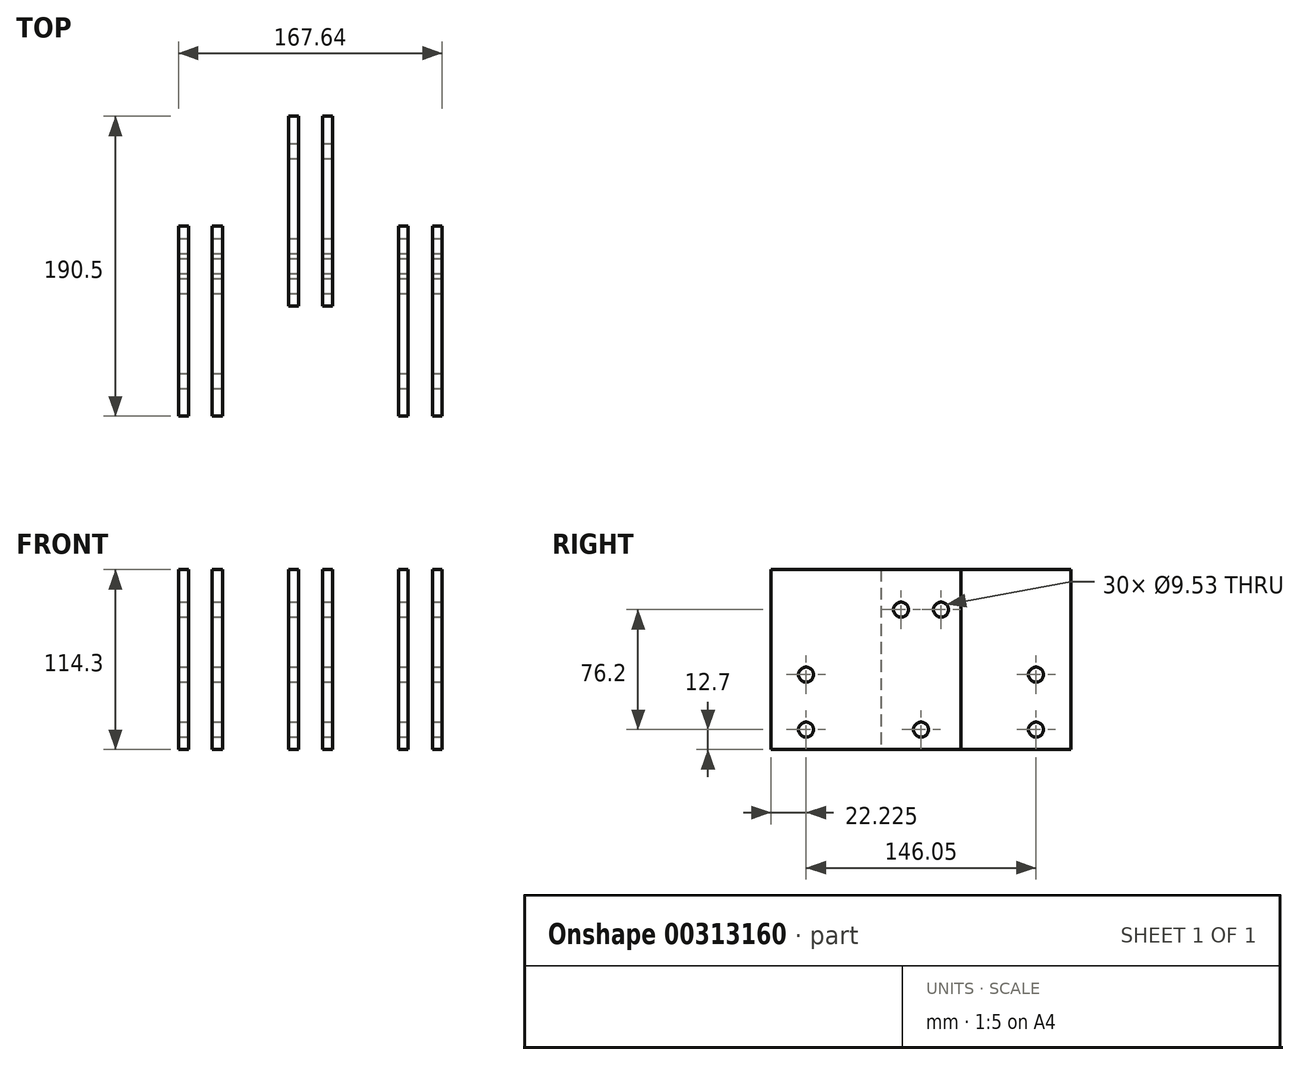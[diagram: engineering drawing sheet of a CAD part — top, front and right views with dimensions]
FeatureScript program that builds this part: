
annotation { "Feature Type Name" : "Feature", "Feature Type Description" : "" }
export const myFeature = defineFeature(function(context is Context, id is Id, definition is map)
    precondition{}
    {
        {
            var Q0;
            Q0=qCreatedBy(makeId("Top.planeOp"),FACE);
            var sketch = newSketch(context, id + "F0", { "sketchPlane" : qUnion([Q0])});
            skLineSegment(sketch, "E0.bottom", {"start": v(0, 120.65) * mm, "end": v(6.35, 120.65) * mm});
            skLineSegment(sketch, "E0.top", {"start": v(0, 0) * mm, "end": v(6.35, 0) * mm});
            skLineSegment(sketch, "E0.left", {"start": v(0, 120.65) * mm, "end": v(0, 0) * mm});
            skLineSegment(sketch, "E0.right", {"start": v(6.35, 120.65) * mm, "end": v(6.35, 0) * mm});
            skLineSegment(sketch, "E1.bottom", {"start": v(21.6, 120.65) * mm, "end": v(27.94, 120.65) * mm});
            skLineSegment(sketch, "E1.top", {"start": v(21.6, 0) * mm, "end": v(27.94, 0) * mm});
            skLineSegment(sketch, "E1.left", {"start": v(21.6, 120.65) * mm, "end": v(21.6, 0) * mm});
            skLineSegment(sketch, "E1.right", {"start": v(27.94, 120.65) * mm, "end": v(27.94, 0) * mm});
            skLineSegment(sketch, "E2.bottom", {"start": v(-69.85, 190.5) * mm, "end": v(-63.5, 190.5) * mm});
            skLineSegment(sketch, "E2.top", {"start": v(-69.85, 69.85) * mm, "end": v(-63.5, 69.85) * mm});
            skLineSegment(sketch, "E2.left", {"start": v(-69.85, 190.5) * mm, "end": v(-69.85, 69.85) * mm});
            skLineSegment(sketch, "E2.right", {"start": v(-63.5, 190.5) * mm, "end": v(-63.5, 69.85) * mm});
            skLineSegment(sketch, "E3.bottom", {"start": v(-48.26, 190.5) * mm, "end": v(-41.9, 190.5) * mm});
            skLineSegment(sketch, "E3.top", {"start": v(-48.26, 69.85) * mm, "end": v(-41.9, 69.85) * mm});
            skLineSegment(sketch, "E3.left", {"start": v(-48.26, 190.5) * mm, "end": v(-48.26, 69.85) * mm});
            skLineSegment(sketch, "E3.right", {"start": v(-41.9, 190.5) * mm, "end": v(-41.9, 69.85) * mm});
            skLineSegment(sketch, "E4.bottom", {"start": v(-139.7, 120.65) * mm, "end": v(-133.35, 120.65) * mm});
            skLineSegment(sketch, "E4.top", {"start": v(-139.7, 0) * mm, "end": v(-133.35, 0) * mm});
            skLineSegment(sketch, "E4.left", {"start": v(-139.7, 120.65) * mm, "end": v(-139.7, 0) * mm});
            skLineSegment(sketch, "E4.right", {"start": v(-133.35, 120.65) * mm, "end": v(-133.35, 0) * mm});
            skLineSegment(sketch, "E5.bottom", {"start": v(-118.1, 120.65) * mm, "end": v(-111.76, 120.65) * mm});
            skLineSegment(sketch, "E5.top", {"start": v(-118.1, 0) * mm, "end": v(-111.76, 0) * mm});
            skLineSegment(sketch, "E5.left", {"start": v(-118.1, 120.65) * mm, "end": v(-118.1, 0) * mm});
            skLineSegment(sketch, "E5.right", {"start": v(-111.76, 120.65) * mm, "end": v(-111.76, 0) * mm});
            skSolve(sketch);
        }
        {
            var Q0;
            Q0=qSketchRegion(id+"F0",true);
            extrude(context, id + "F1", {"entities" : qUnion([Q0]), "endBound" : BoundingType.SYMMETRIC, "depth" : 114.3 * mm});
        }
        {
            var Q0;
            Q0=qCreatedBy(makeId("Right.planeOp"),FACE);
            var sketch = newSketch(context, id + "F2", { "sketchPlane" : qUnion([Q0])});
            skCircle(sketch, "E6", {"center": v(82.55, 31.75) * mm, "radius": 4.76 * mm});
            skCircle(sketch, "E7", {"center": v(82.55, 6.35) * mm, "radius": 4.76 * mm, "construction": true});
            skCircle(sketch, "E8", {"center": v(168.28, -44.45) * mm, "radius": 4.76 * mm});
            skCircle(sketch, "E9", {"center": v(168.28, -9.52) * mm, "radius": 4.76 * mm});
            skLineSegment(sketch, "E10", {"start": v(95.25, 31.75) * mm, "end": v(95.25, 6.35) * mm, "construction": true});
            skCircle(sketch, "E11.MirrorC", {"center": v(22.23, -44.45) * mm, "radius": 4.76 * mm});
            skCircle(sketch, "E12.MirrorC", {"center": v(22.23, -9.53) * mm, "radius": 4.76 * mm});
            skCircle(sketch, "E13", {"center": v(107.95, 31.75) * mm, "radius": 4.76 * mm});
            skLineSegment(sketch, "E14.bottom", {"start": v(82.55, 31.75) * mm, "end": v(107.95, 31.75) * mm, "construction": true});
            skLineSegment(sketch, "E14.top", {"start": v(82.55, 6.35) * mm, "end": v(107.95, 6.35) * mm, "construction": true});
            skLineSegment(sketch, "E14.left", {"start": v(82.55, 31.75) * mm, "end": v(82.55, 6.35) * mm, "construction": true});
            skLineSegment(sketch, "E14.right", {"start": v(107.95, 31.75) * mm, "end": v(107.95, 6.35) * mm, "construction": true});
            skCircle(sketch, "E15", {"center": v(95.25, -44.45) * mm, "radius": 4.76 * mm});
            skSolve(sketch);
        }
        {
            var Q0;
            Q0 = qSketchRegion(id + "F2", true);
            extrude(context, id + "F3", {"entities" : qUnion([Q0]), "operationType" : NewBodyOperationType.REMOVE, "endBound" : BoundingType.THROUGH_ALL, "oppositeDirection" : true, "depth" : 25.4 * mm, "hasSecondDirection" : true, "secondDirectionBound" : SecondDirectionBoundingType.THROUGH_ALL, "secondDirectionOppositeDirection" : false, "secondDirectionDepth" : 25.4 * mm});
        }
    });
